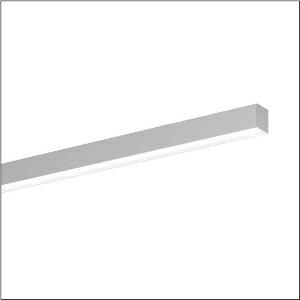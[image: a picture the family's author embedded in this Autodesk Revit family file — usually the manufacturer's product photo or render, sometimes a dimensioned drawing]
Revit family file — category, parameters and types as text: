
# Revit family: silica_r__21_51mx23dc4asb_a1ef
name_source: partatom
category: Lighting Fixtures
units: mm (PartAtom-declared; Revit-internal decimal feet)

## family parameters
Cut with Voids When Loaded = No
Host = Face
Light Source = No
Part Type = Normal
Room Calculation Point = No
Round Connector Dimension = Use Diameter
Shared = No

## types (1)
- --- (1 x LED, 8200 lm, 58.2 W, 4000K)
    Apparent Load = 58 VA
    CIE Flux Codes = 78 96 99 100 100
    Color Rendering = 80
    Color Temperature = 4000K
    Default Elevation = 1800 mm
    Description = Silica® 21, office luminaire, primary optical cover: prismatic diffuser, of PMMA, CAT 2 (L<= 3000cd/m²), light emission: direct distribution, primary light characteristic: symmetric, installation type: surface-mounted, LED, rated luminous flux: 8.200lm, luminous efficacy: 141lm/W, light colour: 840, colour temperature: 4000K, with terminal, 3+2-pole, max. 2.5mm², mains connection: 220..240V, AC, 50/60Hz, rated input power: 58.2W, luminaire housing, of aluminium, metallic grey (RAL 9006), length: 3.004mm, width: 53mm, height: 53mm, protection rating (complete): IP20, insulation class (complete): insulation class I (protective earthing), certification: CE, permissible operating ambient temperature: 0..+35°C, standard: EN 50419, packaging unit: 1 piece
    Height = 0 mm  [stored 0 ft]
    Lamp = 1 x LED
    Lamp Light Flux = 8200 lm
    Lamp Power = 58.2 W
    Lamp count = 1
    Length = 3004 mm
    Luminous efficacy = 141 lm/W
    Manufacturer = Siteco
    ModVariant = No
    Model = 51MX23DC4ASB
    Mounting Place = Ceiling
    Mounting Type = Recessed
    Number of Poles = 1
    OnlyDefault = Yes
    Power Factor = 1
    Product Name = Silica® 21
    Product group = office luminaire | ceiling recessed
    ProductGroupID = 401
    Protection Class = Protection class I
    Protection Degree = IP 20
    RLX_Detail_Level = 1
    RLX_Emergency_Light_Flux = 0 lm
    RLX_Emergency_Type = 0
    RLX_Emergency_Type_DB = No
    RlxData = <blob elided: 21189 chars, md5=63a25a7c>
    Socket = socket
    Standby Power = 0 W
    System Light Flux = 8200 lm
    System Power = 58 W
    Type Comments = factory setting: luminous flux: 100 % | dim-lin: 254 | 323 mA
    Type Image = l_1313588.jpg
    URL = http://relux.com
    VarID = @adj_067771
    Voltage = 0 V
    Weight = 0.00 kg
    Width = 53 mm

note: [stored X ft] marks values corroborated as IEEE doubles in the binary element streams (Revit-internal decimal feet)

## geometry (parser evidence)
native form markers: Blend x4, Sweep x11
no freeform markers — native parametric forms only
